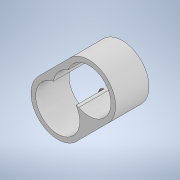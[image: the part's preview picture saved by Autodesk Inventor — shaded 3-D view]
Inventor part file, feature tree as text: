
AUTODESK INVENTOR PART (.ipt)
format: ipt  version: 2020 (Build 240168000, 168)  size: 208,896 bytes
history: native  units: in
note: dims shown in document units (in); Inventor stores cm internally (conversion verified against a paired STEP export)
features: extrude x4, sketch x4, fillet x2
ambient origin geometry x8: Origin, YZ Plane, XZ Plane, XY Plane, X Axis, Y Axis, Z Axis, Center Point
bodies: Solid1 (feature_tree)
feature tree (10):
  extrude  "Extrusion1"  Depth=0.9606in
  extrude  "Extrusion3"  TaperAngle=45.0deg  [1 undecoded]
  extrude  "Extrusion4"  Depth=0.4134in
  extrude  "Extrusion5"  Depth=0.1181in
  fillet  "Fillet1"  Radius=0.1181in
  fillet  "Fillet2"  Radius=0.1181in
  sketch  "Sketch1"  dims[d0=0.9724in d1=0.9606in]
  sketch  "Sketch3"  dims[d2=0.0in d3=45.0deg]
  sketch  "Sketch4"  dims[d4=0.0in d5=0.4134in]
  sketch  "Sketch5"  dims[d20=0.3346in d21=0.1181in d22=0.1181in d23=0.1181in d24=0.9606in d25=0.9606in d26=0.1772in d27=0.1181in d28=0.0in d32=0.9724in d33=0.9606in d34=0.0in d35=45.0deg d36=0.0in d37=0.4134in d38=0.3346in d39=0.1181in d40=0.1181in d41=0.1181in d42=0.9606in d43=0.9606in d44=0.1772in d45=0.6102in d46=0.0in d49=0.2165in d50=0.0787in d51=0.0394in d52=0.0in d53=0.0in d54=0.9724in d55=0.9606in d56=0.0in d57=45.0deg d58=0.0in d59=0.4134in d60=0.3346in d61=0.1181in d62=0.1181in d63=0.1181in d64=0.9606in d65=0.9606in d66=0.1772in d67=0.5827in d68=0.5827in d69=1.1654in d70=0.5827in d71=0.7283in d72=0.0in d73=0.1181in d74=0.1181in]
note: 1 required parameter value undecoded (feature->parameter linkage not recoverable at this tier; creation-order binding heuristic only, values carry confidence <= 0.55)
